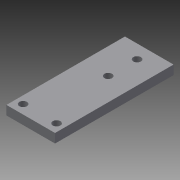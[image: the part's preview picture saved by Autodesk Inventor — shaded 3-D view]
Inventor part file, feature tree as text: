
AUTODESK INVENTOR PART (.ipt)
format: ipt  version: 2014 SP1 (Build 180222100, 222)  size: 87,040 bytes
history: native  units: mm
features: extrude x1, sketch x1
ambient origin geometry x8: Origin, YZ Plane, XZ Plane, XY Plane, X Axis, Y Axis, Z Axis, Center Point
bodies: Solid1 (feature_tree)
feature tree (2):
  extrude  "Extrusion1"  Depth=39.0mm
  sketch  "Sketch1"  dims[d0=16.0mm d1=39.0mm d2=3.0mm d3=5.5mm d4=11.0mm d5=2.5mm d6=2.5mm d7=25.0mm d8=9.5mm d9=7.5mm d10=2.5mm d11=2.5mm d12=3.0mm d13=0.0mm]
